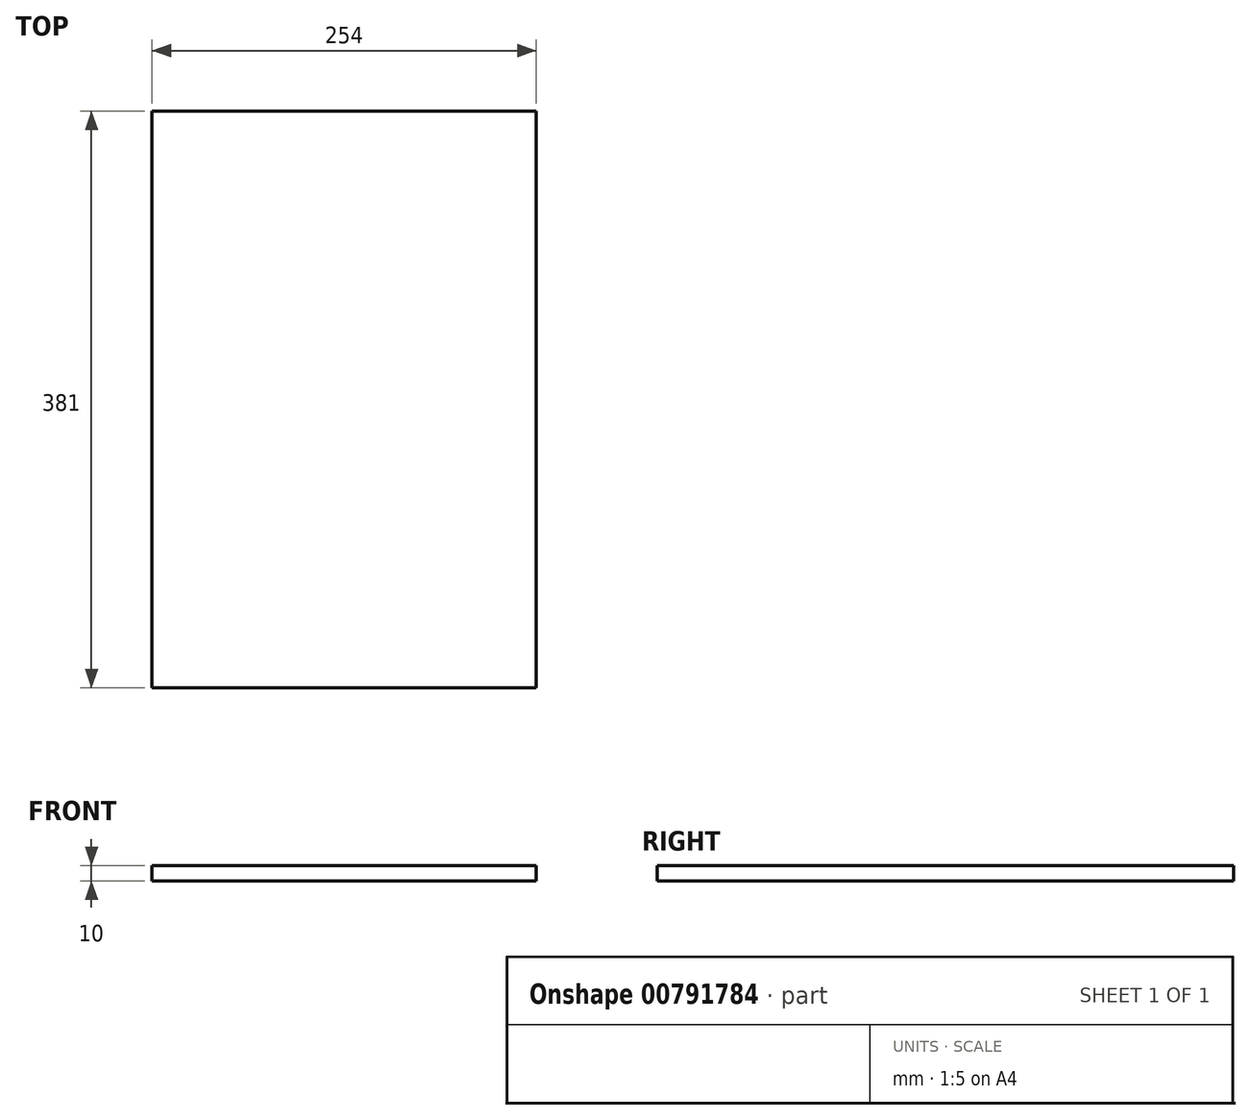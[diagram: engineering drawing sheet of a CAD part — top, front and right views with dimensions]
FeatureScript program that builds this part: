
annotation { "Feature Type Name" : "Feature", "Feature Type Description" : "" }
export const myFeature = defineFeature(function(context is Context, id is Id, definition is map)
    precondition{}
    {
        {
            var Q0;
            Q0=qCreatedBy(makeId("Top.planeOp"),FACE);
            var sketch = newSketch(context, id + "F0", { "sketchPlane" : qUnion([Q0])});
            skLineSegment(sketch, "E0.bottom", {"start": v(-125.1, 284.5) * mm, "end": v(128.9, 284.5) * mm});
            skLineSegment(sketch, "E0.top", {"start": v(-125.1, -96.5) * mm, "end": v(128.9, -96.5) * mm});
            skLineSegment(sketch, "E0.left", {"start": v(-125.1, 284.5) * mm, "end": v(-125.1, -96.5) * mm});
            skLineSegment(sketch, "E0.right", {"start": v(128.9, 284.5) * mm, "end": v(128.9, -96.5) * mm});
            skSolve(sketch);
        }
        {
            var Q0;
            Q0=makeQuery(id+"F0.imprint","IMPRINT",FACE,{"disambiguationData":[TD([[makeQuery(id+"F0.imprint","IMPRINT",EDGE,{"derivedFrom":sQuery(id+"F0.wireOp",EDGE,"E0.bottom")}),-1.0]])]});
            extrude(context, id + "F1", {"entities" : qUnion([Q0]), "endBound" : BoundingType.SYMMETRIC, "depth" : 10 * mm, "offsetDistance" : 25.4 * mm});
        }
    });
